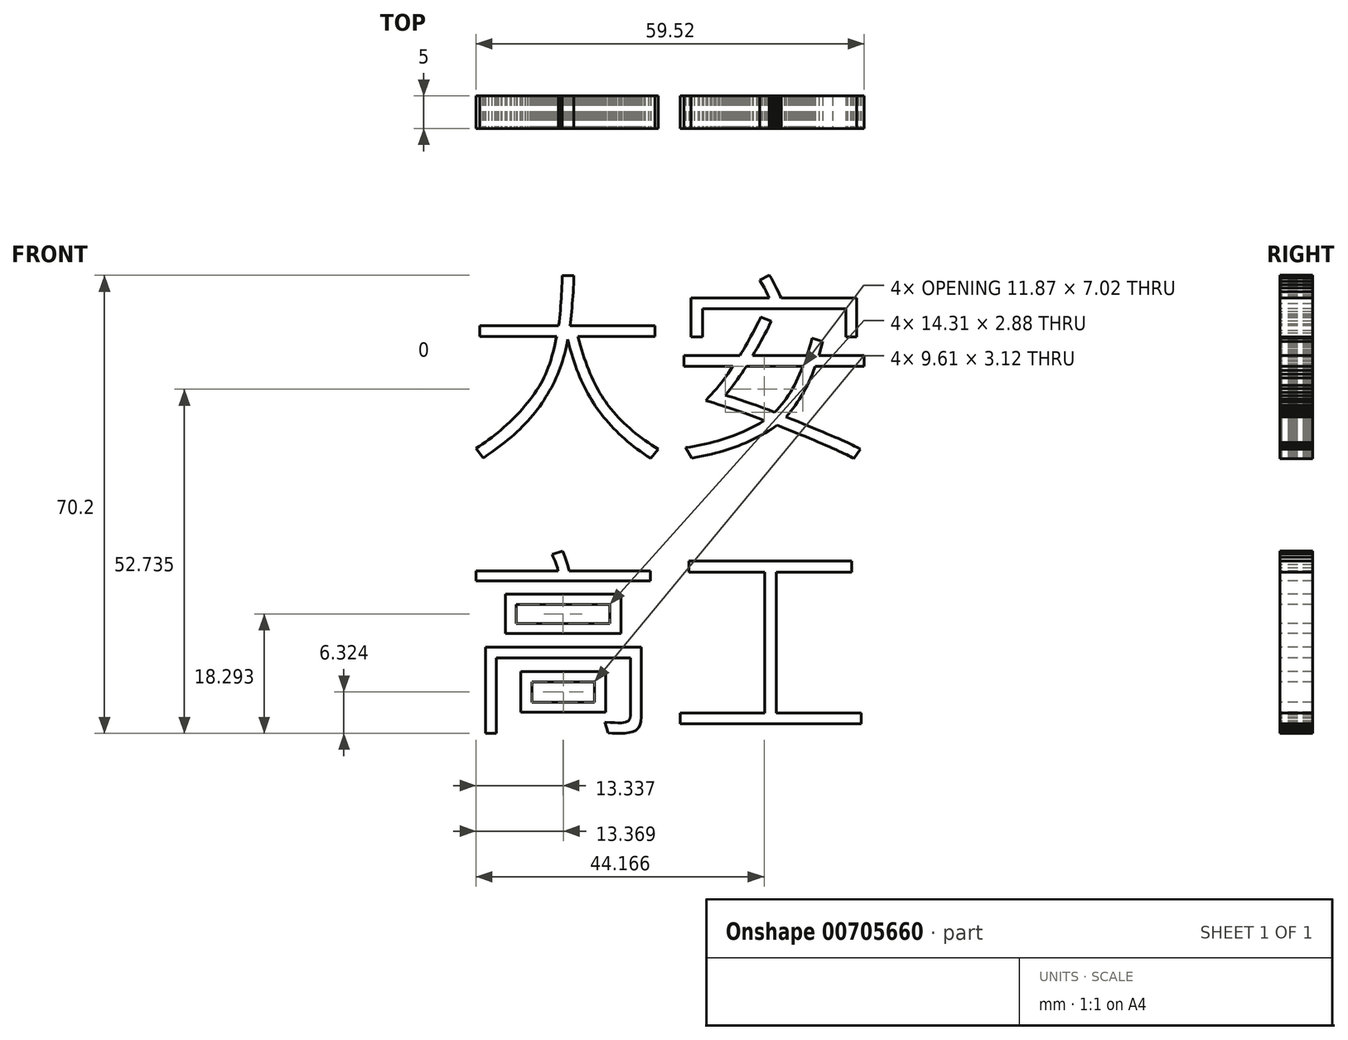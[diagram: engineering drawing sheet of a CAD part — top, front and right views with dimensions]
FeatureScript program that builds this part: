
annotation { "Feature Type Name" : "Feature", "Feature Type Description" : "" }
export const myFeature = defineFeature(function(context is Context, id is Id, definition is map)
    precondition{}
    {
        {
            var Q0;
            Q0=qCreatedBy(makeId("Front.planeOp"),FACE);
            var sketch = newSketch(context, id + "F0", { "sketchPlane" : qUnion([Q0])});
            skLineSegment(sketch, "E0", {"start": v(-17.49, 25.35) * mm, "end": v(-17.63, 24.66) * mm});
            skLineSegment(sketch, "E1", {"start": v(-17.63, 24.66) * mm, "end": v(-17.79, 24) * mm});
            skLineSegment(sketch, "E2", {"start": v(-17.79, 24) * mm, "end": v(-17.95, 23.34) * mm});
            skLineSegment(sketch, "E3", {"start": v(-17.95, 23.34) * mm, "end": v(-18.12, 22.72) * mm});
            skLineSegment(sketch, "E4", {"start": v(-18.12, 22.72) * mm, "end": v(-18.3, 22.11) * mm});
            skLineSegment(sketch, "E5", {"start": v(-18.3, 22.11) * mm, "end": v(-18.5, 21.54) * mm});
            skLineSegment(sketch, "E6", {"start": v(-18.5, 21.54) * mm, "end": v(-18.69, 20.98) * mm});
            skLineSegment(sketch, "E7", {"start": v(-18.69, 20.98) * mm, "end": v(-18.9, 20.45) * mm});
            skLineSegment(sketch, "E8", {"start": v(-18.9, 20.45) * mm, "end": v(-19.11, 19.94) * mm});
            skLineSegment(sketch, "E9", {"start": v(-19.11, 19.94) * mm, "end": v(-19.33, 19.45) * mm});
            skLineSegment(sketch, "E10", {"start": v(-19.33, 19.45) * mm, "end": v(-19.56, 18.99) * mm});
            skLineSegment(sketch, "E11", {"start": v(-19.56, 18.99) * mm, "end": v(-19.8, 18.54) * mm});
            skLineSegment(sketch, "E12", {"start": v(-19.8, 18.54) * mm, "end": v(-20.05, 18.13) * mm});
            skLineSegment(sketch, "E13", {"start": v(-20.05, 18.13) * mm, "end": v(-20.17, 17.94) * mm});
            skLineSegment(sketch, "E14", {"start": v(-20.17, 17.94) * mm, "end": v(-20.48, 17.46) * mm});
            skLineSegment(sketch, "E15", {"start": v(-20.48, 17.46) * mm, "end": v(-20.8, 16.98) * mm});
            skLineSegment(sketch, "E16", {"start": v(-20.8, 16.98) * mm, "end": v(-21.14, 16.5) * mm});
            skLineSegment(sketch, "E17", {"start": v(-21.14, 16.5) * mm, "end": v(-21.5, 16.03) * mm});
            skLineSegment(sketch, "E18", {"start": v(-21.5, 16.03) * mm, "end": v(-21.86, 15.56) * mm});
            skLineSegment(sketch, "E19", {"start": v(-21.86, 15.56) * mm, "end": v(-22.24, 15.1) * mm});
            skLineSegment(sketch, "E20", {"start": v(-22.24, 15.1) * mm, "end": v(-22.64, 14.65) * mm});
            skLineSegment(sketch, "E21", {"start": v(-22.64, 14.65) * mm, "end": v(-23.05, 14.19) * mm});
            skLineSegment(sketch, "E22", {"start": v(-23.05, 14.19) * mm, "end": v(-23.47, 13.74) * mm});
            skLineSegment(sketch, "E23", {"start": v(-23.47, 13.74) * mm, "end": v(-23.9, 13.3) * mm});
            skLineSegment(sketch, "E24", {"start": v(-23.9, 13.3) * mm, "end": v(-24.36, 12.86) * mm});
            skLineSegment(sketch, "E25", {"start": v(-24.36, 12.86) * mm, "end": v(-24.58, 12.64) * mm});
            skLineSegment(sketch, "E26", {"start": v(-24.58, 12.64) * mm, "end": v(-25.04, 12.21) * mm});
            skLineSegment(sketch, "E27", {"start": v(-25.04, 12.21) * mm, "end": v(-25.5, 11.8) * mm});
            skLineSegment(sketch, "E28", {"start": v(-25.5, 11.8) * mm, "end": v(-25.96, 11.4) * mm});
            skLineSegment(sketch, "E29", {"start": v(-25.96, 11.4) * mm, "end": v(-26.42, 11.01) * mm});
            skLineSegment(sketch, "E30", {"start": v(-26.42, 11.01) * mm, "end": v(-26.9, 10.63) * mm});
            skLineSegment(sketch, "E31", {"start": v(-26.9, 10.63) * mm, "end": v(-27.36, 10.26) * mm});
            skLineSegment(sketch, "E32", {"start": v(-27.36, 10.26) * mm, "end": v(-27.84, 9.9) * mm});
            skLineSegment(sketch, "E33", {"start": v(-27.84, 9.9) * mm, "end": v(-28.31, 9.56) * mm});
            skLineSegment(sketch, "E34", {"start": v(-28.31, 9.56) * mm, "end": v(-28.8, 9.22) * mm});
            skLineSegment(sketch, "E35", {"start": v(-28.8, 9.22) * mm, "end": v(-29.28, 8.9) * mm});
            skLineSegment(sketch, "E36", {"start": v(-29.28, 8.9) * mm, "end": v(-29.76, 8.58) * mm});
            skLineSegment(sketch, "E37", {"start": v(-29.76, 8.58) * mm, "end": v(-28.68, 7.14) * mm});
            skLineSegment(sketch, "E38", {"start": v(-28.68, 7.14) * mm, "end": v(-28.46, 7.28) * mm});
            skLineSegment(sketch, "E39", {"start": v(-28.46, 7.28) * mm, "end": v(-27.9, 7.64) * mm});
            skLineSegment(sketch, "E40", {"start": v(-27.9, 7.64) * mm, "end": v(-27.36, 8) * mm});
            skLineSegment(sketch, "E41", {"start": v(-27.36, 8) * mm, "end": v(-26.84, 8.38) * mm});
            skLineSegment(sketch, "E42", {"start": v(-26.84, 8.38) * mm, "end": v(-26.33, 8.75) * mm});
            skLineSegment(sketch, "E43", {"start": v(-26.33, 8.75) * mm, "end": v(-25.82, 9.13) * mm});
            skLineSegment(sketch, "E44", {"start": v(-25.82, 9.13) * mm, "end": v(-25.33, 9.52) * mm});
            skLineSegment(sketch, "E45", {"start": v(-25.33, 9.52) * mm, "end": v(-24.85, 9.91) * mm});
            skLineSegment(sketch, "E46", {"start": v(-24.85, 9.91) * mm, "end": v(-24.38, 10.3) * mm});
            skLineSegment(sketch, "E47", {"start": v(-24.38, 10.3) * mm, "end": v(-23.92, 10.7) * mm});
            skLineSegment(sketch, "E48", {"start": v(-23.92, 10.7) * mm, "end": v(-23.48, 11.12) * mm});
            skLineSegment(sketch, "E49", {"start": v(-23.48, 11.12) * mm, "end": v(-23.05, 11.53) * mm});
            skLineSegment(sketch, "E50", {"start": v(-23.05, 11.53) * mm, "end": v(-22.63, 11.95) * mm});
            skLineSegment(sketch, "E51", {"start": v(-22.63, 11.95) * mm, "end": v(-22.22, 12.37) * mm});
            skLineSegment(sketch, "E52", {"start": v(-22.22, 12.37) * mm, "end": v(-21.82, 12.8) * mm});
            skLineSegment(sketch, "E53", {"start": v(-21.82, 12.8) * mm, "end": v(-21.44, 13.24) * mm});
            skLineSegment(sketch, "E54", {"start": v(-21.44, 13.24) * mm, "end": v(-21.06, 13.68) * mm});
            skLineSegment(sketch, "E55", {"start": v(-21.06, 13.68) * mm, "end": v(-20.7, 14.12) * mm});
            skLineSegment(sketch, "E56", {"start": v(-20.7, 14.12) * mm, "end": v(-20.35, 14.57) * mm});
            skLineSegment(sketch, "E57", {"start": v(-20.35, 14.57) * mm, "end": v(-20.01, 15.03) * mm});
            skLineSegment(sketch, "E58", {"start": v(-20.01, 15.03) * mm, "end": v(-19.69, 15.49) * mm});
            skLineSegment(sketch, "E59", {"start": v(-19.69, 15.49) * mm, "end": v(-19.37, 15.96) * mm});
            skLineSegment(sketch, "E60", {"start": v(-19.37, 15.96) * mm, "end": v(-19.07, 16.43) * mm});
            skLineSegment(sketch, "E61", {"start": v(-19.07, 16.43) * mm, "end": v(-18.78, 16.9) * mm});
            skLineSegment(sketch, "E62", {"start": v(-18.78, 16.9) * mm, "end": v(-18.5, 17.39) * mm});
            skLineSegment(sketch, "E63", {"start": v(-18.5, 17.39) * mm, "end": v(-18.23, 17.87) * mm});
            skLineSegment(sketch, "E64", {"start": v(-18.23, 17.87) * mm, "end": v(-17.97, 18.37) * mm});
            skLineSegment(sketch, "E65", {"start": v(-17.97, 18.37) * mm, "end": v(-17.72, 18.86) * mm});
            skLineSegment(sketch, "E66", {"start": v(-17.72, 18.86) * mm, "end": v(-17.5, 19.37) * mm});
            skLineSegment(sketch, "E67", {"start": v(-17.5, 19.37) * mm, "end": v(-17.27, 19.88) * mm});
            skLineSegment(sketch, "E68", {"start": v(-17.27, 19.88) * mm, "end": v(-17.07, 20.4) * mm});
            skLineSegment(sketch, "E69", {"start": v(-17.07, 20.4) * mm, "end": v(-16.86, 20.91) * mm});
            skLineSegment(sketch, "E70", {"start": v(-16.86, 20.91) * mm, "end": v(-16.68, 21.44) * mm});
            skLineSegment(sketch, "E71", {"start": v(-16.68, 21.44) * mm, "end": v(-16.5, 21.97) * mm});
            skLineSegment(sketch, "E72", {"start": v(-16.5, 21.97) * mm, "end": v(-16.35, 22.5) * mm});
            skLineSegment(sketch, "E73", {"start": v(-16.35, 22.5) * mm, "end": v(-16.2, 23.05) * mm});
            skLineSegment(sketch, "E74", {"start": v(-16.2, 23.05) * mm, "end": v(-16.06, 23.6) * mm});
            skLineSegment(sketch, "E75", {"start": v(-16.06, 23.6) * mm, "end": v(-15.93, 24.15) * mm});
            skLineSegment(sketch, "E76", {"start": v(-15.93, 24.15) * mm, "end": v(-15.81, 24.7) * mm});
            skLineSegment(sketch, "E77", {"start": v(-15.81, 24.7) * mm, "end": v(-15.71, 25.27) * mm});
            skLineSegment(sketch, "E78", {"start": v(27.82, -8.66) * mm, "end": v(2.88, -8.66) * mm});
            skLineSegment(sketch, "E79", {"start": v(2.88, -8.66) * mm, "end": v(2.88, -10.4) * mm});
            skLineSegment(sketch, "E80", {"start": v(2.88, -10.4) * mm, "end": v(14.53, -10.4) * mm});
            skLineSegment(sketch, "E81", {"start": v(14.53, -10.4) * mm, "end": v(14.53, -32.02) * mm});
            skLineSegment(sketch, "E82", {"start": v(14.53, -32.02) * mm, "end": v(1.55, -32.02) * mm});
            skLineSegment(sketch, "E83", {"start": v(1.55, -32.02) * mm, "end": v(1.55, -33.67) * mm});
            skLineSegment(sketch, "E84", {"start": v(1.55, -33.67) * mm, "end": v(29.28, -33.67) * mm});
            skLineSegment(sketch, "E85", {"start": v(29.28, -33.67) * mm, "end": v(29.28, -32.02) * mm});
            skLineSegment(sketch, "E86", {"start": v(29.28, -32.02) * mm, "end": v(16.25, -32.02) * mm});
            skLineSegment(sketch, "E87", {"start": v(16.25, -32.02) * mm, "end": v(16.25, -10.4) * mm});
            skLineSegment(sketch, "E88", {"start": v(16.25, -10.4) * mm, "end": v(27.82, -10.4) * mm});
            skLineSegment(sketch, "E89", {"start": v(27.82, -10.4) * mm, "end": v(27.82, -8.66) * mm});
            skLineSegment(sketch, "E90", {"start": v(-16.5, -7.17) * mm, "end": v(-18.11, -7.68) * mm});
            skLineSegment(sketch, "E91", {"start": v(-18.11, -7.68) * mm, "end": v(-17.94, -8.05) * mm});
            skLineSegment(sketch, "E92", {"start": v(-17.94, -8.05) * mm, "end": v(-17.66, -8.7) * mm});
            skLineSegment(sketch, "E93", {"start": v(-17.66, -8.7) * mm, "end": v(-17.44, -9.28) * mm});
            skLineSegment(sketch, "E94", {"start": v(-17.44, -9.28) * mm, "end": v(-17.29, -9.78) * mm});
            skLineSegment(sketch, "E95", {"start": v(-17.29, -9.78) * mm, "end": v(-17.2, -10.22) * mm});
            skLineSegment(sketch, "E96", {"start": v(-17.2, -10.22) * mm, "end": v(-29.76, -10.22) * mm});
            skLineSegment(sketch, "E97", {"start": v(-29.76, -10.22) * mm, "end": v(-29.76, -11.74) * mm});
            skLineSegment(sketch, "E98", {"start": v(-29.76, -11.74) * mm, "end": v(-3.06, -11.74) * mm});
            skLineSegment(sketch, "E99", {"start": v(-3.06, -11.74) * mm, "end": v(-3.06, -10.22) * mm});
            skLineSegment(sketch, "E100", {"start": v(-3.06, -10.22) * mm, "end": v(-15.48, -10.22) * mm});
            skLineSegment(sketch, "E101", {"start": v(-15.48, -10.22) * mm, "end": v(-15.55, -9.95) * mm});
            skLineSegment(sketch, "E102", {"start": v(-15.55, -9.95) * mm, "end": v(-15.73, -9.28) * mm});
            skLineSegment(sketch, "E103", {"start": v(-15.73, -9.28) * mm, "end": v(-15.91, -8.66) * mm});
            skLineSegment(sketch, "E104", {"start": v(-15.91, -8.66) * mm, "end": v(-16.1, -8.1) * mm});
            skLineSegment(sketch, "E105", {"start": v(-16.1, -8.1) * mm, "end": v(-16.3, -7.6) * mm});
            skLineSegment(sketch, "E106", {"start": v(-16.3, -7.6) * mm, "end": v(-16.5, -7.17) * mm});
            skLineSegment(sketch, "E107", {"start": v(-9.27, -15.37) * mm, "end": v(-9.27, -18.25) * mm});
            skLineSegment(sketch, "E108", {"start": v(-9.27, -18.25) * mm, "end": v(-23.58, -18.25) * mm});
            skLineSegment(sketch, "E109", {"start": v(-25.29, -19.8) * mm, "end": v(-7.51, -19.8) * mm});
            skLineSegment(sketch, "E110", {"start": v(-7.51, -19.8) * mm, "end": v(-7.51, -13.77) * mm});
            skLineSegment(sketch, "E111", {"start": v(-7.51, -13.77) * mm, "end": v(-25.29, -13.77) * mm});
            skLineSegment(sketch, "E112", {"start": v(-25.29, -13.77) * mm, "end": v(-25.29, -19.8) * mm});
            skLineSegment(sketch, "E113", {"start": v(-23.58, -18.25) * mm, "end": v(-23.58, -15.37) * mm});
            skLineSegment(sketch, "E114", {"start": v(-23.58, -15.37) * mm, "end": v(-9.27, -15.37) * mm});
            skLineSegment(sketch, "E115", {"start": v(-6.06, -23.52) * mm, "end": v(-6.06, -32.33) * mm});
            skLineSegment(sketch, "E116", {"start": v(-6.06, -32.33) * mm, "end": v(-6.13, -32.79) * mm});
            skLineSegment(sketch, "E117", {"start": v(-6.13, -32.79) * mm, "end": v(-6.38, -33.18) * mm});
            skLineSegment(sketch, "E118", {"start": v(-6.38, -33.18) * mm, "end": v(-6.82, -33.42) * mm});
            skLineSegment(sketch, "E119", {"start": v(-6.82, -33.42) * mm, "end": v(-7.46, -33.5) * mm});
            skLineSegment(sketch, "E120", {"start": v(-4.63, -33.83) * mm, "end": v(-4.47, -33.27) * mm});
            skLineSegment(sketch, "E121", {"start": v(-4.47, -33.27) * mm, "end": v(-4.42, -32.63) * mm});
            skLineSegment(sketch, "E122", {"start": v(-4.42, -32.63) * mm, "end": v(-4.42, -21.92) * mm});
            skLineSegment(sketch, "E123", {"start": v(-4.42, -21.92) * mm, "end": v(-28.3, -21.92) * mm});
            skLineSegment(sketch, "E124", {"start": v(-28.3, -21.92) * mm, "end": v(-28.3, -35.1) * mm});
            skLineSegment(sketch, "E125", {"start": v(-28.3, -35.1) * mm, "end": v(-26.68, -35.1) * mm});
            skLineSegment(sketch, "E126", {"start": v(-26.68, -35.1) * mm, "end": v(-26.68, -23.52) * mm});
            skLineSegment(sketch, "E127", {"start": v(-26.68, -23.52) * mm, "end": v(-6.06, -23.52) * mm});
            skLineSegment(sketch, "E128", {"start": v(-11.59, -27.22) * mm, "end": v(-11.59, -30.33) * mm});
            skLineSegment(sketch, "E129", {"start": v(-11.59, -30.33) * mm, "end": v(-21.2, -30.33) * mm});
            skLineSegment(sketch, "E130", {"start": v(-22.91, -31.87) * mm, "end": v(-9.9, -31.87) * mm});
            skLineSegment(sketch, "E131", {"start": v(-9.9, -31.87) * mm, "end": v(-9.9, -25.67) * mm});
            skLineSegment(sketch, "E132", {"start": v(-9.9, -25.67) * mm, "end": v(-22.91, -25.67) * mm});
            skLineSegment(sketch, "E133", {"start": v(-22.91, -25.67) * mm, "end": v(-22.91, -31.87) * mm});
            skLineSegment(sketch, "E134", {"start": v(-21.2, -30.33) * mm, "end": v(-21.2, -27.22) * mm});
            skLineSegment(sketch, "E135", {"start": v(-21.2, -27.22) * mm, "end": v(-11.59, -27.22) * mm});
            skLineSegment(sketch, "E136", {"start": v(-10.02, -33.42) * mm, "end": v(-9.48, -35.06) * mm});
            skLineSegment(sketch, "E137", {"start": v(-9.48, -35.06) * mm, "end": v(-8.88, -35.09) * mm});
            skLineSegment(sketch, "E138", {"start": v(-8.88, -35.09) * mm, "end": v(-8.28, -35.1) * mm});
            skLineSegment(sketch, "E139", {"start": v(-8.28, -35.1) * mm, "end": v(-7.75, -35.1) * mm});
            skLineSegment(sketch, "E140", {"start": v(-7.75, -35.1) * mm, "end": v(-6.95, -35.08) * mm});
            skLineSegment(sketch, "E141", {"start": v(-6.95, -35.08) * mm, "end": v(-6.26, -35) * mm});
            skLineSegment(sketch, "E142", {"start": v(-6.26, -35) * mm, "end": v(-5.71, -34.86) * mm});
            skLineSegment(sketch, "E143", {"start": v(-5.71, -34.86) * mm, "end": v(-5.28, -34.67) * mm});
            skLineSegment(sketch, "E144", {"start": v(-5.28, -34.67) * mm, "end": v(-5, -34.42) * mm});
            skLineSegment(sketch, "E145", {"start": v(-5, -34.42) * mm, "end": v(-4.9, -34.3) * mm});
            skLineSegment(sketch, "E146", {"start": v(-4.9, -34.3) * mm, "end": v(-4.63, -33.83) * mm});
            skLineSegment(sketch, "E147", {"start": v(-7.46, -33.5) * mm, "end": v(-7.54, -33.5) * mm});
            skLineSegment(sketch, "E148", {"start": v(-7.54, -33.5) * mm, "end": v(-7.96, -33.49) * mm});
            skLineSegment(sketch, "E149", {"start": v(-7.96, -33.49) * mm, "end": v(-8.5, -33.48) * mm});
            skLineSegment(sketch, "E150", {"start": v(-8.5, -33.48) * mm, "end": v(-9.2, -33.45) * mm});
            skLineSegment(sketch, "E151", {"start": v(-9.2, -33.45) * mm, "end": v(-10.02, -33.42) * mm});
            skLineSegment(sketch, "E152", {"start": v(15.23, 35.1) * mm, "end": v(13.7, 34.38) * mm});
            skLineSegment(sketch, "E153", {"start": v(13.7, 34.38) * mm, "end": v(13.8, 34.24) * mm});
            skLineSegment(sketch, "E154", {"start": v(13.8, 34.24) * mm, "end": v(14.1, 33.73) * mm});
            skLineSegment(sketch, "E155", {"start": v(14.1, 33.73) * mm, "end": v(14.4, 33.2) * mm});
            skLineSegment(sketch, "E156", {"start": v(14.4, 33.2) * mm, "end": v(14.7, 32.68) * mm});
            skLineSegment(sketch, "E157", {"start": v(14.7, 32.68) * mm, "end": v(14.97, 32.15) * mm});
            skLineSegment(sketch, "E158", {"start": v(14.97, 32.15) * mm, "end": v(15.23, 31.6) * mm});
            skLineSegment(sketch, "E159", {"start": v(15.23, 31.6) * mm, "end": v(3.2, 31.6) * mm});
            skLineSegment(sketch, "E160", {"start": v(3.2, 31.6) * mm, "end": v(3.2, 25.64) * mm});
            skLineSegment(sketch, "E161", {"start": v(3.2, 25.64) * mm, "end": v(4.96, 25.64) * mm});
            skLineSegment(sketch, "E162", {"start": v(4.96, 25.64) * mm, "end": v(4.96, 29.96) * mm});
            skLineSegment(sketch, "E163", {"start": v(4.96, 29.96) * mm, "end": v(26.94, 29.96) * mm});
            skLineSegment(sketch, "E164", {"start": v(28.61, 31.6) * mm, "end": v(17, 31.6) * mm});
            skLineSegment(sketch, "E165", {"start": v(17, 31.6) * mm, "end": v(16.85, 31.96) * mm});
            skLineSegment(sketch, "E166", {"start": v(16.85, 31.96) * mm, "end": v(16.58, 32.57) * mm});
            skLineSegment(sketch, "E167", {"start": v(16.58, 32.57) * mm, "end": v(16.3, 33.15) * mm});
            skLineSegment(sketch, "E168", {"start": v(16.3, 33.15) * mm, "end": v(16.03, 33.7) * mm});
            skLineSegment(sketch, "E169", {"start": v(16.03, 33.7) * mm, "end": v(15.76, 34.2) * mm});
            skLineSegment(sketch, "E170", {"start": v(15.76, 34.2) * mm, "end": v(15.5, 34.67) * mm});
            skLineSegment(sketch, "E171", {"start": v(15.5, 34.67) * mm, "end": v(15.23, 35.1) * mm});
            skLineSegment(sketch, "E172", {"start": v(-14.75, 35.07) * mm, "end": v(-16.56, 35.07) * mm});
            skLineSegment(sketch, "E173", {"start": v(-16.56, 35.07) * mm, "end": v(-16.57, 34.55) * mm});
            skLineSegment(sketch, "E174", {"start": v(-16.57, 34.55) * mm, "end": v(-16.59, 33.96) * mm});
            skLineSegment(sketch, "E175", {"start": v(-16.59, 33.96) * mm, "end": v(-16.6, 33.37) * mm});
            skLineSegment(sketch, "E176", {"start": v(-16.6, 33.37) * mm, "end": v(-16.63, 32.77) * mm});
            skLineSegment(sketch, "E177", {"start": v(-16.63, 32.77) * mm, "end": v(-16.66, 32.17) * mm});
            skLineSegment(sketch, "E178", {"start": v(-16.66, 32.17) * mm, "end": v(-16.7, 31.58) * mm});
            skLineSegment(sketch, "E179", {"start": v(-16.7, 31.58) * mm, "end": v(-16.74, 30.98) * mm});
            skLineSegment(sketch, "E180", {"start": v(-16.74, 30.98) * mm, "end": v(-16.79, 30.38) * mm});
            skLineSegment(sketch, "E181", {"start": v(-16.79, 30.38) * mm, "end": v(-16.84, 29.77) * mm});
            skLineSegment(sketch, "E182", {"start": v(-16.84, 29.77) * mm, "end": v(-16.9, 29.17) * mm});
            skLineSegment(sketch, "E183", {"start": v(-16.9, 29.17) * mm, "end": v(-16.96, 28.57) * mm});
            skLineSegment(sketch, "E184", {"start": v(-16.96, 28.57) * mm, "end": v(-17.03, 27.96) * mm});
            skLineSegment(sketch, "E185", {"start": v(-17.03, 27.96) * mm, "end": v(-17.1, 27.36) * mm});
            skLineSegment(sketch, "E186", {"start": v(-17.1, 27.36) * mm, "end": v(-29.19, 27.36) * mm});
            skLineSegment(sketch, "E187", {"start": v(-29.19, 27.36) * mm, "end": v(-29.19, 25.72) * mm});
            skLineSegment(sketch, "E188", {"start": v(-29.19, 25.72) * mm, "end": v(-17.41, 25.72) * mm});
            skLineSegment(sketch, "E189", {"start": v(-17.41, 25.72) * mm, "end": v(-17.49, 25.35) * mm});
            skLineSegment(sketch, "E190", {"start": v(-15.71, 25.27) * mm, "end": v(-15.63, 24.93) * mm});
            skLineSegment(sketch, "E191", {"start": v(-15.63, 24.93) * mm, "end": v(-15.47, 24.3) * mm});
            skLineSegment(sketch, "E192", {"start": v(-15.47, 24.3) * mm, "end": v(-15.3, 23.66) * mm});
            skLineSegment(sketch, "E193", {"start": v(-15.3, 23.66) * mm, "end": v(-15.12, 23.04) * mm});
            skLineSegment(sketch, "E194", {"start": v(-15.12, 23.04) * mm, "end": v(-14.93, 22.44) * mm});
            skLineSegment(sketch, "E195", {"start": v(-14.93, 22.44) * mm, "end": v(-14.73, 21.84) * mm});
            skLineSegment(sketch, "E196", {"start": v(-14.73, 21.84) * mm, "end": v(-14.53, 21.25) * mm});
            skLineSegment(sketch, "E197", {"start": v(-14.53, 21.25) * mm, "end": v(-14.32, 20.68) * mm});
            skLineSegment(sketch, "E198", {"start": v(-14.32, 20.68) * mm, "end": v(-14.1, 20.12) * mm});
            skLineSegment(sketch, "E199", {"start": v(-14.1, 20.12) * mm, "end": v(-13.87, 19.56) * mm});
            skLineSegment(sketch, "E200", {"start": v(-13.87, 19.56) * mm, "end": v(-13.64, 19.02) * mm});
            skLineSegment(sketch, "E201", {"start": v(-13.64, 19.02) * mm, "end": v(-13.4, 18.49) * mm});
            skLineSegment(sketch, "E202", {"start": v(-13.4, 18.49) * mm, "end": v(-13.14, 17.96) * mm});
            skLineSegment(sketch, "E203", {"start": v(-13.14, 17.96) * mm, "end": v(-12.88, 17.46) * mm});
            skLineSegment(sketch, "E204", {"start": v(-12.88, 17.46) * mm, "end": v(-12.61, 16.96) * mm});
            skLineSegment(sketch, "E205", {"start": v(-12.61, 16.96) * mm, "end": v(-12.33, 16.47) * mm});
            skLineSegment(sketch, "E206", {"start": v(-12.33, 16.47) * mm, "end": v(-12.04, 16) * mm});
            skLineSegment(sketch, "E207", {"start": v(-12.04, 16) * mm, "end": v(-11.75, 15.52) * mm});
            skLineSegment(sketch, "E208", {"start": v(-11.75, 15.52) * mm, "end": v(-11.45, 15.07) * mm});
            skLineSegment(sketch, "E209", {"start": v(-11.45, 15.07) * mm, "end": v(-11.14, 14.62) * mm});
            skLineSegment(sketch, "E210", {"start": v(-11.14, 14.62) * mm, "end": v(-10.89, 14.28) * mm});
            skLineSegment(sketch, "E211", {"start": v(-10.89, 14.28) * mm, "end": v(-10.55, 13.82) * mm});
            skLineSegment(sketch, "E212", {"start": v(-10.55, 13.82) * mm, "end": v(-10.2, 13.38) * mm});
            skLineSegment(sketch, "E213", {"start": v(-10.2, 13.38) * mm, "end": v(-9.83, 12.94) * mm});
            skLineSegment(sketch, "E214", {"start": v(-9.83, 12.94) * mm, "end": v(-9.46, 12.5) * mm});
            skLineSegment(sketch, "E215", {"start": v(-9.46, 12.5) * mm, "end": v(-9.07, 12.08) * mm});
            skLineSegment(sketch, "E216", {"start": v(-9.07, 12.08) * mm, "end": v(-8.67, 11.65) * mm});
            skLineSegment(sketch, "E217", {"start": v(-8.67, 11.65) * mm, "end": v(-8.26, 11.23) * mm});
            skLineSegment(sketch, "E218", {"start": v(-8.26, 11.23) * mm, "end": v(-7.84, 10.82) * mm});
            skLineSegment(sketch, "E219", {"start": v(-7.84, 10.82) * mm, "end": v(-7.4, 10.42) * mm});
            skLineSegment(sketch, "E220", {"start": v(-7.4, 10.42) * mm, "end": v(-6.96, 10.02) * mm});
            skLineSegment(sketch, "E221", {"start": v(-6.96, 10.02) * mm, "end": v(-6.5, 9.63) * mm});
            skLineSegment(sketch, "E222", {"start": v(-6.5, 9.63) * mm, "end": v(-6.04, 9.24) * mm});
            skLineSegment(sketch, "E223", {"start": v(-6.04, 9.24) * mm, "end": v(-5.56, 8.86) * mm});
            skLineSegment(sketch, "E224", {"start": v(-5.56, 8.86) * mm, "end": v(-5.06, 8.49) * mm});
            skLineSegment(sketch, "E225", {"start": v(-5.06, 8.49) * mm, "end": v(-4.56, 8.12) * mm});
            skLineSegment(sketch, "E226", {"start": v(-4.56, 8.12) * mm, "end": v(-4.04, 7.75) * mm});
            skLineSegment(sketch, "E227", {"start": v(-4.04, 7.75) * mm, "end": v(-3.51, 7.4) * mm});
            skLineSegment(sketch, "E228", {"start": v(-3.51, 7.4) * mm, "end": v(-2.98, 7.05) * mm});
            skLineSegment(sketch, "E229", {"start": v(-2.98, 7.05) * mm, "end": v(-1.84, 8.47) * mm});
            skLineSegment(sketch, "E230", {"start": v(-1.84, 8.47) * mm, "end": v(-2.34, 8.77) * mm});
            skLineSegment(sketch, "E231", {"start": v(-2.34, 8.77) * mm, "end": v(-2.86, 9.1) * mm});
            skLineSegment(sketch, "E232", {"start": v(-2.86, 9.1) * mm, "end": v(-3.38, 9.45) * mm});
            skLineSegment(sketch, "E233", {"start": v(-3.38, 9.45) * mm, "end": v(-3.88, 9.8) * mm});
            skLineSegment(sketch, "E234", {"start": v(-3.88, 9.8) * mm, "end": v(-4.37, 10.16) * mm});
            skLineSegment(sketch, "E235", {"start": v(-4.37, 10.16) * mm, "end": v(-4.86, 10.52) * mm});
            skLineSegment(sketch, "E236", {"start": v(-4.86, 10.52) * mm, "end": v(-5.33, 10.9) * mm});
            skLineSegment(sketch, "E237", {"start": v(-5.33, 10.9) * mm, "end": v(-5.79, 11.28) * mm});
            skLineSegment(sketch, "E238", {"start": v(-5.79, 11.28) * mm, "end": v(-6.24, 11.67) * mm});
            skLineSegment(sketch, "E239", {"start": v(-6.24, 11.67) * mm, "end": v(-6.67, 12.07) * mm});
            skLineSegment(sketch, "E240", {"start": v(-6.67, 12.07) * mm, "end": v(-7.1, 12.47) * mm});
            skLineSegment(sketch, "E241", {"start": v(-7.1, 12.47) * mm, "end": v(-7.51, 12.9) * mm});
            skLineSegment(sketch, "E242", {"start": v(-7.51, 12.9) * mm, "end": v(-7.92, 13.31) * mm});
            skLineSegment(sketch, "E243", {"start": v(-7.92, 13.31) * mm, "end": v(-8.3, 13.74) * mm});
            skLineSegment(sketch, "E244", {"start": v(-8.3, 13.74) * mm, "end": v(-8.7, 14.18) * mm});
            skLineSegment(sketch, "E245", {"start": v(-8.7, 14.18) * mm, "end": v(-9.06, 14.62) * mm});
            skLineSegment(sketch, "E246", {"start": v(-9.06, 14.62) * mm, "end": v(-9.42, 15.07) * mm});
            skLineSegment(sketch, "E247", {"start": v(-9.42, 15.07) * mm, "end": v(-9.6, 15.32) * mm});
            skLineSegment(sketch, "E248", {"start": v(-9.6, 15.32) * mm, "end": v(-9.9, 15.73) * mm});
            skLineSegment(sketch, "E249", {"start": v(-9.9, 15.73) * mm, "end": v(-10.2, 16.15) * mm});
            skLineSegment(sketch, "E250", {"start": v(-10.2, 16.15) * mm, "end": v(-10.48, 16.6) * mm});
            skLineSegment(sketch, "E251", {"start": v(-10.48, 16.6) * mm, "end": v(-10.76, 17.05) * mm});
            skLineSegment(sketch, "E252", {"start": v(-10.76, 17.05) * mm, "end": v(-11.03, 17.52) * mm});
            skLineSegment(sketch, "E253", {"start": v(-11.03, 17.52) * mm, "end": v(-11.3, 18) * mm});
            skLineSegment(sketch, "E254", {"start": v(-11.3, 18) * mm, "end": v(-11.55, 18.5) * mm});
            skLineSegment(sketch, "E255", {"start": v(-11.55, 18.5) * mm, "end": v(-11.8, 19.02) * mm});
            skLineSegment(sketch, "E256", {"start": v(-11.8, 19.02) * mm, "end": v(-12.04, 19.55) * mm});
            skLineSegment(sketch, "E257", {"start": v(-12.04, 19.55) * mm, "end": v(-12.28, 20.1) * mm});
            skLineSegment(sketch, "E258", {"start": v(-12.28, 20.1) * mm, "end": v(-12.51, 20.67) * mm});
            skLineSegment(sketch, "E259", {"start": v(-12.51, 20.67) * mm, "end": v(-12.74, 21.24) * mm});
            skLineSegment(sketch, "E260", {"start": v(-12.74, 21.24) * mm, "end": v(-12.95, 21.83) * mm});
            skLineSegment(sketch, "E261", {"start": v(-12.95, 21.83) * mm, "end": v(-13.16, 22.44) * mm});
            skLineSegment(sketch, "E262", {"start": v(-13.16, 22.44) * mm, "end": v(-13.37, 23.07) * mm});
            skLineSegment(sketch, "E263", {"start": v(-13.37, 23.07) * mm, "end": v(-13.56, 23.7) * mm});
            skLineSegment(sketch, "E264", {"start": v(-13.56, 23.7) * mm, "end": v(-13.75, 24.36) * mm});
            skLineSegment(sketch, "E265", {"start": v(-13.75, 24.36) * mm, "end": v(-13.94, 25.03) * mm});
            skLineSegment(sketch, "E266", {"start": v(-13.94, 25.03) * mm, "end": v(-14.12, 25.72) * mm});
            skLineSegment(sketch, "E267", {"start": v(-14.12, 25.72) * mm, "end": v(-2.36, 25.72) * mm});
            skLineSegment(sketch, "E268", {"start": v(-2.36, 25.72) * mm, "end": v(-2.36, 27.36) * mm});
            skLineSegment(sketch, "E269", {"start": v(-2.36, 27.36) * mm, "end": v(-15.35, 27.36) * mm});
            skLineSegment(sketch, "E270", {"start": v(-15.35, 27.36) * mm, "end": v(-15.3, 27.85) * mm});
            skLineSegment(sketch, "E271", {"start": v(-15.3, 27.85) * mm, "end": v(-15.23, 28.41) * mm});
            skLineSegment(sketch, "E272", {"start": v(-15.23, 28.41) * mm, "end": v(-15.17, 28.98) * mm});
            skLineSegment(sketch, "E273", {"start": v(-15.17, 28.98) * mm, "end": v(-15.1, 29.56) * mm});
            skLineSegment(sketch, "E274", {"start": v(-15.1, 29.56) * mm, "end": v(-15.06, 30.14) * mm});
            skLineSegment(sketch, "E275", {"start": v(-15.06, 30.14) * mm, "end": v(-15, 30.73) * mm});
            skLineSegment(sketch, "E276", {"start": v(-15, 30.73) * mm, "end": v(-14.96, 31.33) * mm});
            skLineSegment(sketch, "E277", {"start": v(-14.96, 31.33) * mm, "end": v(-14.91, 31.94) * mm});
            skLineSegment(sketch, "E278", {"start": v(-14.91, 31.94) * mm, "end": v(-14.87, 32.55) * mm});
            skLineSegment(sketch, "E279", {"start": v(-14.87, 32.55) * mm, "end": v(-14.84, 33.17) * mm});
            skLineSegment(sketch, "E280", {"start": v(-14.84, 33.17) * mm, "end": v(-14.8, 33.8) * mm});
            skLineSegment(sketch, "E281", {"start": v(-14.8, 33.8) * mm, "end": v(-14.77, 34.43) * mm});
            skLineSegment(sketch, "E282", {"start": v(-14.77, 34.43) * mm, "end": v(-14.75, 35.07) * mm});
            skLineSegment(sketch, "E283", {"start": v(26.94, 29.96) * mm, "end": v(26.94, 25.64) * mm});
            skLineSegment(sketch, "E284", {"start": v(26.94, 25.64) * mm, "end": v(28.61, 25.64) * mm});
            skLineSegment(sketch, "E285", {"start": v(28.61, 25.64) * mm, "end": v(28.61, 31.6) * mm});
            skLineSegment(sketch, "E286", {"start": v(13.9, 28.69) * mm, "end": v(13.83, 28.56) * mm});
            skLineSegment(sketch, "E287", {"start": v(13.83, 28.56) * mm, "end": v(13.53, 27.96) * mm});
            skLineSegment(sketch, "E288", {"start": v(13.53, 27.96) * mm, "end": v(13.25, 27.38) * mm});
            skLineSegment(sketch, "E289", {"start": v(13.25, 27.38) * mm, "end": v(12.95, 26.81) * mm});
            skLineSegment(sketch, "E290", {"start": v(12.95, 26.81) * mm, "end": v(12.66, 26.26) * mm});
            skLineSegment(sketch, "E291", {"start": v(12.66, 26.26) * mm, "end": v(12.37, 25.72) * mm});
            skLineSegment(sketch, "E292", {"start": v(12.37, 25.72) * mm, "end": v(12.08, 25.2) * mm});
            skLineSegment(sketch, "E293", {"start": v(12.08, 25.2) * mm, "end": v(11.8, 24.68) * mm});
            skLineSegment(sketch, "E294", {"start": v(11.8, 24.68) * mm, "end": v(11.5, 24.19) * mm});
            skLineSegment(sketch, "E295", {"start": v(11.5, 24.19) * mm, "end": v(11.22, 23.7) * mm});
            skLineSegment(sketch, "E296", {"start": v(11.22, 23.7) * mm, "end": v(10.94, 23.24) * mm});
            skLineSegment(sketch, "E297", {"start": v(10.94, 23.24) * mm, "end": v(10.66, 22.8) * mm});
            skLineSegment(sketch, "E298", {"start": v(12.66, 22.8) * mm, "end": v(12.66, 22.8) * mm});
            skLineSegment(sketch, "E299", {"start": v(12.66, 22.8) * mm, "end": v(13, 23.38) * mm});
            skLineSegment(sketch, "E300", {"start": v(13, 23.38) * mm, "end": v(13.33, 23.95) * mm});
            skLineSegment(sketch, "E301", {"start": v(13.33, 23.95) * mm, "end": v(13.64, 24.5) * mm});
            skLineSegment(sketch, "E302", {"start": v(13.64, 24.5) * mm, "end": v(13.94, 25.05) * mm});
            skLineSegment(sketch, "E303", {"start": v(13.94, 25.05) * mm, "end": v(14.23, 25.58) * mm});
            skLineSegment(sketch, "E304", {"start": v(14.23, 25.58) * mm, "end": v(14.52, 26.1) * mm});
            skLineSegment(sketch, "E305", {"start": v(14.52, 26.1) * mm, "end": v(14.79, 26.62) * mm});
            skLineSegment(sketch, "E306", {"start": v(14.79, 26.62) * mm, "end": v(15.04, 27.12) * mm});
            skLineSegment(sketch, "E307", {"start": v(15.04, 27.12) * mm, "end": v(15.29, 27.61) * mm});
            skLineSegment(sketch, "E308", {"start": v(15.29, 27.61) * mm, "end": v(15.52, 28.08) * mm});
            skLineSegment(sketch, "E309", {"start": v(15.52, 28.08) * mm, "end": v(13.9, 28.69) * mm});
            skLineSegment(sketch, "E310", {"start": v(21.77, 25.45) * mm, "end": v(21.7, 25.12) * mm});
            skLineSegment(sketch, "E311", {"start": v(21.7, 25.12) * mm, "end": v(21.55, 24.58) * mm});
            skLineSegment(sketch, "E312", {"start": v(21.55, 24.58) * mm, "end": v(21.38, 24) * mm});
            skLineSegment(sketch, "E313", {"start": v(21.38, 24) * mm, "end": v(21.2, 23.4) * mm});
            skLineSegment(sketch, "E314", {"start": v(21.2, 23.4) * mm, "end": v(20.97, 22.8) * mm});
            skLineSegment(sketch, "E315", {"start": v(20.97, 22.8) * mm, "end": v(12.66, 22.8) * mm});
            skLineSegment(sketch, "E316", {"start": v(10.66, 22.8) * mm, "end": v(2.09, 22.8) * mm});
            skLineSegment(sketch, "E317", {"start": v(2.09, 22.8) * mm, "end": v(2.09, 21.14) * mm});
            skLineSegment(sketch, "E318", {"start": v(2.09, 21.14) * mm, "end": v(9.62, 21.14) * mm});
            skLineSegment(sketch, "E319", {"start": v(20.34, 21.14) * mm, "end": v(20.11, 20.55) * mm});
            skLineSegment(sketch, "E320", {"start": v(20.11, 20.55) * mm, "end": v(19.86, 19.94) * mm});
            skLineSegment(sketch, "E321", {"start": v(19.86, 19.94) * mm, "end": v(19.6, 19.36) * mm});
            skLineSegment(sketch, "E322", {"start": v(19.6, 19.36) * mm, "end": v(19.33, 18.78) * mm});
            skLineSegment(sketch, "E323", {"start": v(19.33, 18.78) * mm, "end": v(19.05, 18.23) * mm});
            skLineSegment(sketch, "E324", {"start": v(19.05, 18.23) * mm, "end": v(18.76, 17.7) * mm});
            skLineSegment(sketch, "E325", {"start": v(18.76, 17.7) * mm, "end": v(18.45, 17.18) * mm});
            skLineSegment(sketch, "E326", {"start": v(18.45, 17.18) * mm, "end": v(18.13, 16.7) * mm});
            skLineSegment(sketch, "E327", {"start": v(18.13, 16.7) * mm, "end": v(17.81, 16.22) * mm});
            skLineSegment(sketch, "E328", {"start": v(17.81, 16.22) * mm, "end": v(17.48, 15.76) * mm});
            skLineSegment(sketch, "E329", {"start": v(17.48, 15.76) * mm, "end": v(17.12, 15.33) * mm});
            skLineSegment(sketch, "E330", {"start": v(17.12, 15.33) * mm, "end": v(16.77, 14.9) * mm});
            skLineSegment(sketch, "E331", {"start": v(16.77, 14.9) * mm, "end": v(16.4, 14.5) * mm});
            skLineSegment(sketch, "E332", {"start": v(16.4, 14.5) * mm, "end": v(16.02, 14.13) * mm});
            skLineSegment(sketch, "E333", {"start": v(11.42, 13.96) * mm, "end": v(11.96, 13.77) * mm});
            skLineSegment(sketch, "E334", {"start": v(11.96, 13.77) * mm, "end": v(12.48, 13.58) * mm});
            skLineSegment(sketch, "E335", {"start": v(12.48, 13.58) * mm, "end": v(13, 13.39) * mm});
            skLineSegment(sketch, "E336", {"start": v(13, 13.39) * mm, "end": v(13.49, 13.2) * mm});
            skLineSegment(sketch, "E337", {"start": v(13.49, 13.2) * mm, "end": v(13.97, 13.01) * mm});
            skLineSegment(sketch, "E338", {"start": v(13.97, 13.01) * mm, "end": v(14.43, 12.83) * mm});
            skLineSegment(sketch, "E339", {"start": v(14.43, 12.83) * mm, "end": v(14.2, 12.68) * mm});
            skLineSegment(sketch, "E340", {"start": v(14.2, 12.68) * mm, "end": v(13.72, 12.4) * mm});
            skLineSegment(sketch, "E341", {"start": v(13.72, 12.4) * mm, "end": v(13.23, 12.13) * mm});
            skLineSegment(sketch, "E342", {"start": v(13.23, 12.13) * mm, "end": v(12.74, 11.86) * mm});
            skLineSegment(sketch, "E343", {"start": v(12.74, 11.86) * mm, "end": v(12.23, 11.6) * mm});
            skLineSegment(sketch, "E344", {"start": v(12.23, 11.6) * mm, "end": v(11.73, 11.37) * mm});
            skLineSegment(sketch, "E345", {"start": v(11.73, 11.37) * mm, "end": v(11.2, 11.13) * mm});
            skLineSegment(sketch, "E346", {"start": v(11.2, 11.13) * mm, "end": v(10.68, 10.9) * mm});
            skLineSegment(sketch, "E347", {"start": v(10.68, 10.9) * mm, "end": v(10.14, 10.69) * mm});
            skLineSegment(sketch, "E348", {"start": v(10.14, 10.69) * mm, "end": v(9.6, 10.48) * mm});
            skLineSegment(sketch, "E349", {"start": v(9.6, 10.48) * mm, "end": v(9.04, 10.28) * mm});
            skLineSegment(sketch, "E350", {"start": v(9.04, 10.28) * mm, "end": v(8.48, 10.1) * mm});
            skLineSegment(sketch, "E351", {"start": v(8.48, 10.1) * mm, "end": v(7.9, 9.91) * mm});
            skLineSegment(sketch, "E352", {"start": v(7.9, 9.91) * mm, "end": v(7.32, 9.74) * mm});
            skLineSegment(sketch, "E353", {"start": v(7.32, 9.74) * mm, "end": v(6.73, 9.58) * mm});
            skLineSegment(sketch, "E354", {"start": v(6.73, 9.58) * mm, "end": v(6.14, 9.43) * mm});
            skLineSegment(sketch, "E355", {"start": v(6.14, 9.43) * mm, "end": v(5.53, 9.28) * mm});
            skLineSegment(sketch, "E356", {"start": v(5.53, 9.28) * mm, "end": v(4.92, 9.15) * mm});
            skLineSegment(sketch, "E357", {"start": v(4.92, 9.15) * mm, "end": v(4.3, 9.02) * mm});
            skLineSegment(sketch, "E358", {"start": v(4.3, 9.02) * mm, "end": v(3.67, 8.9) * mm});
            skLineSegment(sketch, "E359", {"start": v(3.67, 8.9) * mm, "end": v(3.03, 8.8) * mm});
            skLineSegment(sketch, "E360", {"start": v(3.03, 8.8) * mm, "end": v(2.38, 8.7) * mm});
            skLineSegment(sketch, "E361", {"start": v(2.38, 8.7) * mm, "end": v(3.3, 7.08) * mm});
            skLineSegment(sketch, "E362", {"start": v(3.3, 7.08) * mm, "end": v(3.82, 7.17) * mm});
            skLineSegment(sketch, "E363", {"start": v(3.82, 7.17) * mm, "end": v(4.47, 7.3) * mm});
            skLineSegment(sketch, "E364", {"start": v(4.47, 7.3) * mm, "end": v(5.11, 7.42) * mm});
            skLineSegment(sketch, "E365", {"start": v(5.11, 7.42) * mm, "end": v(5.75, 7.56) * mm});
            skLineSegment(sketch, "E366", {"start": v(5.75, 7.56) * mm, "end": v(6.37, 7.7) * mm});
            skLineSegment(sketch, "E367", {"start": v(6.37, 7.7) * mm, "end": v(6.99, 7.86) * mm});
            skLineSegment(sketch, "E368", {"start": v(6.99, 7.86) * mm, "end": v(7.6, 8.02) * mm});
            skLineSegment(sketch, "E369", {"start": v(7.6, 8.02) * mm, "end": v(8.19, 8.2) * mm});
            skLineSegment(sketch, "E370", {"start": v(8.19, 8.2) * mm, "end": v(8.77, 8.38) * mm});
            skLineSegment(sketch, "E371", {"start": v(8.77, 8.38) * mm, "end": v(9.35, 8.57) * mm});
            skLineSegment(sketch, "E372", {"start": v(9.35, 8.57) * mm, "end": v(9.91, 8.77) * mm});
            skLineSegment(sketch, "E373", {"start": v(9.91, 8.77) * mm, "end": v(10.47, 8.98) * mm});
            skLineSegment(sketch, "E374", {"start": v(10.47, 8.98) * mm, "end": v(11.02, 9.19) * mm});
            skLineSegment(sketch, "E375", {"start": v(11.02, 9.19) * mm, "end": v(11.56, 9.42) * mm});
            skLineSegment(sketch, "E376", {"start": v(11.56, 9.42) * mm, "end": v(12.08, 9.65) * mm});
            skLineSegment(sketch, "E377", {"start": v(12.08, 9.65) * mm, "end": v(12.6, 9.89) * mm});
            skLineSegment(sketch, "E378", {"start": v(12.6, 9.89) * mm, "end": v(13.11, 10.14) * mm});
            skLineSegment(sketch, "E379", {"start": v(13.11, 10.14) * mm, "end": v(13.61, 10.4) * mm});
            skLineSegment(sketch, "E380", {"start": v(13.61, 10.4) * mm, "end": v(14.1, 10.67) * mm});
            skLineSegment(sketch, "E381", {"start": v(14.1, 10.67) * mm, "end": v(14.58, 10.94) * mm});
            skLineSegment(sketch, "E382", {"start": v(14.58, 10.94) * mm, "end": v(15.05, 11.22) * mm});
            skLineSegment(sketch, "E383", {"start": v(15.05, 11.22) * mm, "end": v(15.51, 11.52) * mm});
            skLineSegment(sketch, "E384", {"start": v(15.51, 11.52) * mm, "end": v(15.96, 11.82) * mm});
            skLineSegment(sketch, "E385", {"start": v(15.96, 11.82) * mm, "end": v(16.4, 12.13) * mm});
            skLineSegment(sketch, "E386", {"start": v(20.39, 12.34) * mm, "end": v(19.55, 12.68) * mm});
            skLineSegment(sketch, "E387", {"start": v(19.55, 12.68) * mm, "end": v(18.68, 13.03) * mm});
            skLineSegment(sketch, "E388", {"start": v(18.68, 13.03) * mm, "end": v(17.77, 13.4) * mm});
            skLineSegment(sketch, "E389", {"start": v(17.77, 13.4) * mm, "end": v(17.8, 13.43) * mm});
            skLineSegment(sketch, "E390", {"start": v(17.8, 13.43) * mm, "end": v(18.17, 13.85) * mm});
            skLineSegment(sketch, "E391", {"start": v(18.17, 13.85) * mm, "end": v(18.53, 14.3) * mm});
            skLineSegment(sketch, "E392", {"start": v(18.53, 14.3) * mm, "end": v(18.87, 14.74) * mm});
            skLineSegment(sketch, "E393", {"start": v(18.87, 14.74) * mm, "end": v(19.21, 15.2) * mm});
            skLineSegment(sketch, "E394", {"start": v(19.21, 15.2) * mm, "end": v(19.54, 15.68) * mm});
            skLineSegment(sketch, "E395", {"start": v(19.54, 15.68) * mm, "end": v(19.86, 16.16) * mm});
            skLineSegment(sketch, "E396", {"start": v(19.86, 16.16) * mm, "end": v(20.17, 16.67) * mm});
            skLineSegment(sketch, "E397", {"start": v(20.17, 16.67) * mm, "end": v(20.46, 17.18) * mm});
            skLineSegment(sketch, "E398", {"start": v(20.46, 17.18) * mm, "end": v(20.75, 17.7) * mm});
            skLineSegment(sketch, "E399", {"start": v(20.75, 17.7) * mm, "end": v(21.03, 18.25) * mm});
            skLineSegment(sketch, "E400", {"start": v(21.03, 18.25) * mm, "end": v(21.29, 18.8) * mm});
            skLineSegment(sketch, "E401", {"start": v(21.29, 18.8) * mm, "end": v(21.55, 19.37) * mm});
            skLineSegment(sketch, "E402", {"start": v(21.55, 19.37) * mm, "end": v(21.79, 19.94) * mm});
            skLineSegment(sketch, "E403", {"start": v(21.79, 19.94) * mm, "end": v(22.02, 20.54) * mm});
            skLineSegment(sketch, "E404", {"start": v(22.02, 20.54) * mm, "end": v(22.24, 21.14) * mm});
            skLineSegment(sketch, "E405", {"start": v(22.24, 21.14) * mm, "end": v(29.76, 21.14) * mm});
            skLineSegment(sketch, "E406", {"start": v(29.76, 21.14) * mm, "end": v(29.76, 22.8) * mm});
            skLineSegment(sketch, "E407", {"start": v(29.76, 22.8) * mm, "end": v(22.79, 22.8) * mm});
            skLineSegment(sketch, "E408", {"start": v(22.79, 22.8) * mm, "end": v(23.38, 24.94) * mm});
            skLineSegment(sketch, "E409", {"start": v(23.38, 24.94) * mm, "end": v(21.77, 25.45) * mm});
            skLineSegment(sketch, "E410", {"start": v(9.62, 21.14) * mm, "end": v(9.57, 21.06) * mm});
            skLineSegment(sketch, "E411", {"start": v(9.57, 21.06) * mm, "end": v(9.24, 20.59) * mm});
            skLineSegment(sketch, "E412", {"start": v(9.24, 20.59) * mm, "end": v(8.92, 20.1) * mm});
            skLineSegment(sketch, "E413", {"start": v(8.92, 20.1) * mm, "end": v(8.58, 19.63) * mm});
            skLineSegment(sketch, "E414", {"start": v(8.58, 19.63) * mm, "end": v(8.23, 19.15) * mm});
            skLineSegment(sketch, "E415", {"start": v(8.23, 19.15) * mm, "end": v(7.87, 18.69) * mm});
            skLineSegment(sketch, "E416", {"start": v(7.87, 18.69) * mm, "end": v(7.49, 18.21) * mm});
            skLineSegment(sketch, "E417", {"start": v(7.49, 18.21) * mm, "end": v(7.1, 17.75) * mm});
            skLineSegment(sketch, "E418", {"start": v(7.1, 17.75) * mm, "end": v(6.7, 17.28) * mm});
            skLineSegment(sketch, "E419", {"start": v(6.7, 17.28) * mm, "end": v(6.3, 16.82) * mm});
            skLineSegment(sketch, "E420", {"start": v(6.3, 16.82) * mm, "end": v(5.88, 16.37) * mm});
            skLineSegment(sketch, "E421", {"start": v(5.88, 16.37) * mm, "end": v(5.45, 15.9) * mm});
            skLineSegment(sketch, "E422", {"start": v(5.45, 15.9) * mm, "end": v(6, 15.74) * mm});
            skLineSegment(sketch, "E423", {"start": v(6, 15.74) * mm, "end": v(6.65, 15.54) * mm});
            skLineSegment(sketch, "E424", {"start": v(6.65, 15.54) * mm, "end": v(7.3, 15.34) * mm});
            skLineSegment(sketch, "E425", {"start": v(7.3, 15.34) * mm, "end": v(7.92, 15.14) * mm});
            skLineSegment(sketch, "E426", {"start": v(7.92, 15.14) * mm, "end": v(8.54, 14.94) * mm});
            skLineSegment(sketch, "E427", {"start": v(8.54, 14.94) * mm, "end": v(9.15, 14.74) * mm});
            skLineSegment(sketch, "E428", {"start": v(9.15, 14.74) * mm, "end": v(9.74, 14.55) * mm});
            skLineSegment(sketch, "E429", {"start": v(9.74, 14.55) * mm, "end": v(10.3, 14.35) * mm});
            skLineSegment(sketch, "E430", {"start": v(10.3, 14.35) * mm, "end": v(10.87, 14.15) * mm});
            skLineSegment(sketch, "E431", {"start": v(10.87, 14.15) * mm, "end": v(11.42, 13.96) * mm});
            skLineSegment(sketch, "E432", {"start": v(16.02, 14.13) * mm, "end": v(15.82, 14.2) * mm});
            skLineSegment(sketch, "E433", {"start": v(15.82, 14.2) * mm, "end": v(15.14, 14.46) * mm});
            skLineSegment(sketch, "E434", {"start": v(15.14, 14.46) * mm, "end": v(14.48, 14.7) * mm});
            skLineSegment(sketch, "E435", {"start": v(14.48, 14.7) * mm, "end": v(13.84, 14.94) * mm});
            skLineSegment(sketch, "E436", {"start": v(13.84, 14.94) * mm, "end": v(13.22, 15.16) * mm});
            skLineSegment(sketch, "E437", {"start": v(13.22, 15.16) * mm, "end": v(12.62, 15.38) * mm});
            skLineSegment(sketch, "E438", {"start": v(12.62, 15.38) * mm, "end": v(12.03, 15.58) * mm});
            skLineSegment(sketch, "E439", {"start": v(12.03, 15.58) * mm, "end": v(11.47, 15.78) * mm});
            skLineSegment(sketch, "E440", {"start": v(11.47, 15.78) * mm, "end": v(10.92, 15.96) * mm});
            skLineSegment(sketch, "E441", {"start": v(10.92, 15.96) * mm, "end": v(10.4, 16.13) * mm});
            skLineSegment(sketch, "E442", {"start": v(10.4, 16.13) * mm, "end": v(9.89, 16.3) * mm});
            skLineSegment(sketch, "E443", {"start": v(9.89, 16.3) * mm, "end": v(9.4, 16.45) * mm});
            skLineSegment(sketch, "E444", {"start": v(9.4, 16.45) * mm, "end": v(8.93, 16.6) * mm});
            skLineSegment(sketch, "E445", {"start": v(8.93, 16.6) * mm, "end": v(8.47, 16.73) * mm});
            skLineSegment(sketch, "E446", {"start": v(8.47, 16.73) * mm, "end": v(8.5, 16.77) * mm});
            skLineSegment(sketch, "E447", {"start": v(8.5, 16.77) * mm, "end": v(8.87, 17.22) * mm});
            skLineSegment(sketch, "E448", {"start": v(8.87, 17.22) * mm, "end": v(9.23, 17.68) * mm});
            skLineSegment(sketch, "E449", {"start": v(9.23, 17.68) * mm, "end": v(9.59, 18.14) * mm});
            skLineSegment(sketch, "E450", {"start": v(9.59, 18.14) * mm, "end": v(9.94, 18.62) * mm});
            skLineSegment(sketch, "E451", {"start": v(9.94, 18.62) * mm, "end": v(10.3, 19.1) * mm});
            skLineSegment(sketch, "E452", {"start": v(10.3, 19.1) * mm, "end": v(10.64, 19.6) * mm});
            skLineSegment(sketch, "E453", {"start": v(10.64, 19.6) * mm, "end": v(11, 20.1) * mm});
            skLineSegment(sketch, "E454", {"start": v(11, 20.1) * mm, "end": v(11.33, 20.62) * mm});
            skLineSegment(sketch, "E455", {"start": v(11.33, 20.62) * mm, "end": v(11.68, 21.14) * mm});
            skLineSegment(sketch, "E456", {"start": v(11.68, 21.14) * mm, "end": v(20.34, 21.14) * mm});
            skLineSegment(sketch, "E457", {"start": v(16.4, 12.13) * mm, "end": v(16.74, 12) * mm});
            skLineSegment(sketch, "E458", {"start": v(16.74, 12) * mm, "end": v(17.6, 11.65) * mm});
            skLineSegment(sketch, "E459", {"start": v(17.6, 11.65) * mm, "end": v(18.41, 11.33) * mm});
            skLineSegment(sketch, "E460", {"start": v(18.41, 11.33) * mm, "end": v(19.2, 11) * mm});
            skLineSegment(sketch, "E461", {"start": v(19.2, 11) * mm, "end": v(19.96, 10.7) * mm});
            skLineSegment(sketch, "E462", {"start": v(19.96, 10.7) * mm, "end": v(20.7, 10.4) * mm});
            skLineSegment(sketch, "E463", {"start": v(20.7, 10.4) * mm, "end": v(21.4, 10.1) * mm});
            skLineSegment(sketch, "E464", {"start": v(21.4, 10.1) * mm, "end": v(22.06, 9.83) * mm});
            skLineSegment(sketch, "E465", {"start": v(22.06, 9.83) * mm, "end": v(22.7, 9.57) * mm});
            skLineSegment(sketch, "E466", {"start": v(22.7, 9.57) * mm, "end": v(23.3, 9.3) * mm});
            skLineSegment(sketch, "E467", {"start": v(23.3, 9.3) * mm, "end": v(23.88, 9.06) * mm});
            skLineSegment(sketch, "E468", {"start": v(23.88, 9.06) * mm, "end": v(24.42, 8.82) * mm});
            skLineSegment(sketch, "E469", {"start": v(24.42, 8.82) * mm, "end": v(24.93, 8.6) * mm});
            skLineSegment(sketch, "E470", {"start": v(24.93, 8.6) * mm, "end": v(25.42, 8.38) * mm});
            skLineSegment(sketch, "E471", {"start": v(25.42, 8.38) * mm, "end": v(25.87, 8.17) * mm});
            skLineSegment(sketch, "E472", {"start": v(25.87, 8.17) * mm, "end": v(26.3, 7.97) * mm});
            skLineSegment(sketch, "E473", {"start": v(26.3, 7.97) * mm, "end": v(26.68, 7.79) * mm});
            skLineSegment(sketch, "E474", {"start": v(26.68, 7.79) * mm, "end": v(27.05, 7.61) * mm});
            skLineSegment(sketch, "E475", {"start": v(27.05, 7.61) * mm, "end": v(27.38, 7.45) * mm});
            skLineSegment(sketch, "E476", {"start": v(27.38, 7.45) * mm, "end": v(27.67, 7.3) * mm});
            skLineSegment(sketch, "E477", {"start": v(27.67, 7.3) * mm, "end": v(27.94, 7.15) * mm});
            skLineSegment(sketch, "E478", {"start": v(27.94, 7.15) * mm, "end": v(28.18, 7.01) * mm});
            skLineSegment(sketch, "E479", {"start": v(28.18, 7.01) * mm, "end": v(29.18, 8.44) * mm});
            skLineSegment(sketch, "E480", {"start": v(29.18, 8.44) * mm, "end": v(29.04, 8.52) * mm});
            skLineSegment(sketch, "E481", {"start": v(29.04, 8.52) * mm, "end": v(28.83, 8.65) * mm});
            skLineSegment(sketch, "E482", {"start": v(28.83, 8.65) * mm, "end": v(28.57, 8.78) * mm});
            skLineSegment(sketch, "E483", {"start": v(28.57, 8.78) * mm, "end": v(28.28, 8.92) * mm});
            skLineSegment(sketch, "E484", {"start": v(28.28, 8.92) * mm, "end": v(27.95, 9.09) * mm});
            skLineSegment(sketch, "E485", {"start": v(27.95, 9.09) * mm, "end": v(27.6, 9.26) * mm});
            skLineSegment(sketch, "E486", {"start": v(27.6, 9.26) * mm, "end": v(27.2, 9.45) * mm});
            skLineSegment(sketch, "E487", {"start": v(27.2, 9.45) * mm, "end": v(26.75, 9.65) * mm});
            skLineSegment(sketch, "E488", {"start": v(26.75, 9.65) * mm, "end": v(26.28, 9.86) * mm});
            skLineSegment(sketch, "E489", {"start": v(26.28, 9.86) * mm, "end": v(25.77, 10.08) * mm});
            skLineSegment(sketch, "E490", {"start": v(25.77, 10.08) * mm, "end": v(25.22, 10.32) * mm});
            skLineSegment(sketch, "E491", {"start": v(25.22, 10.32) * mm, "end": v(24.65, 10.57) * mm});
            skLineSegment(sketch, "E492", {"start": v(24.65, 10.57) * mm, "end": v(24.02, 10.84) * mm});
            skLineSegment(sketch, "E493", {"start": v(24.02, 10.84) * mm, "end": v(23.37, 11.1) * mm});
            skLineSegment(sketch, "E494", {"start": v(23.37, 11.1) * mm, "end": v(22.68, 11.4) * mm});
            skLineSegment(sketch, "E495", {"start": v(22.68, 11.4) * mm, "end": v(21.95, 11.7) * mm});
            skLineSegment(sketch, "E496", {"start": v(21.95, 11.7) * mm, "end": v(21.19, 12.01) * mm});
            skLineSegment(sketch, "E497", {"start": v(21.19, 12.01) * mm, "end": v(20.39, 12.34) * mm});
            skSolve(sketch);
        }
        {
            var Q0;
            Q0 = qSketchRegion(id + "F0", true);
            extrude(context, id + "F1", {"entities" : qUnion([Q0]), "oppositeDirection" : true, "depth" : 5 * mm, "offsetDistance" : 25 * mm});
        }
    });
